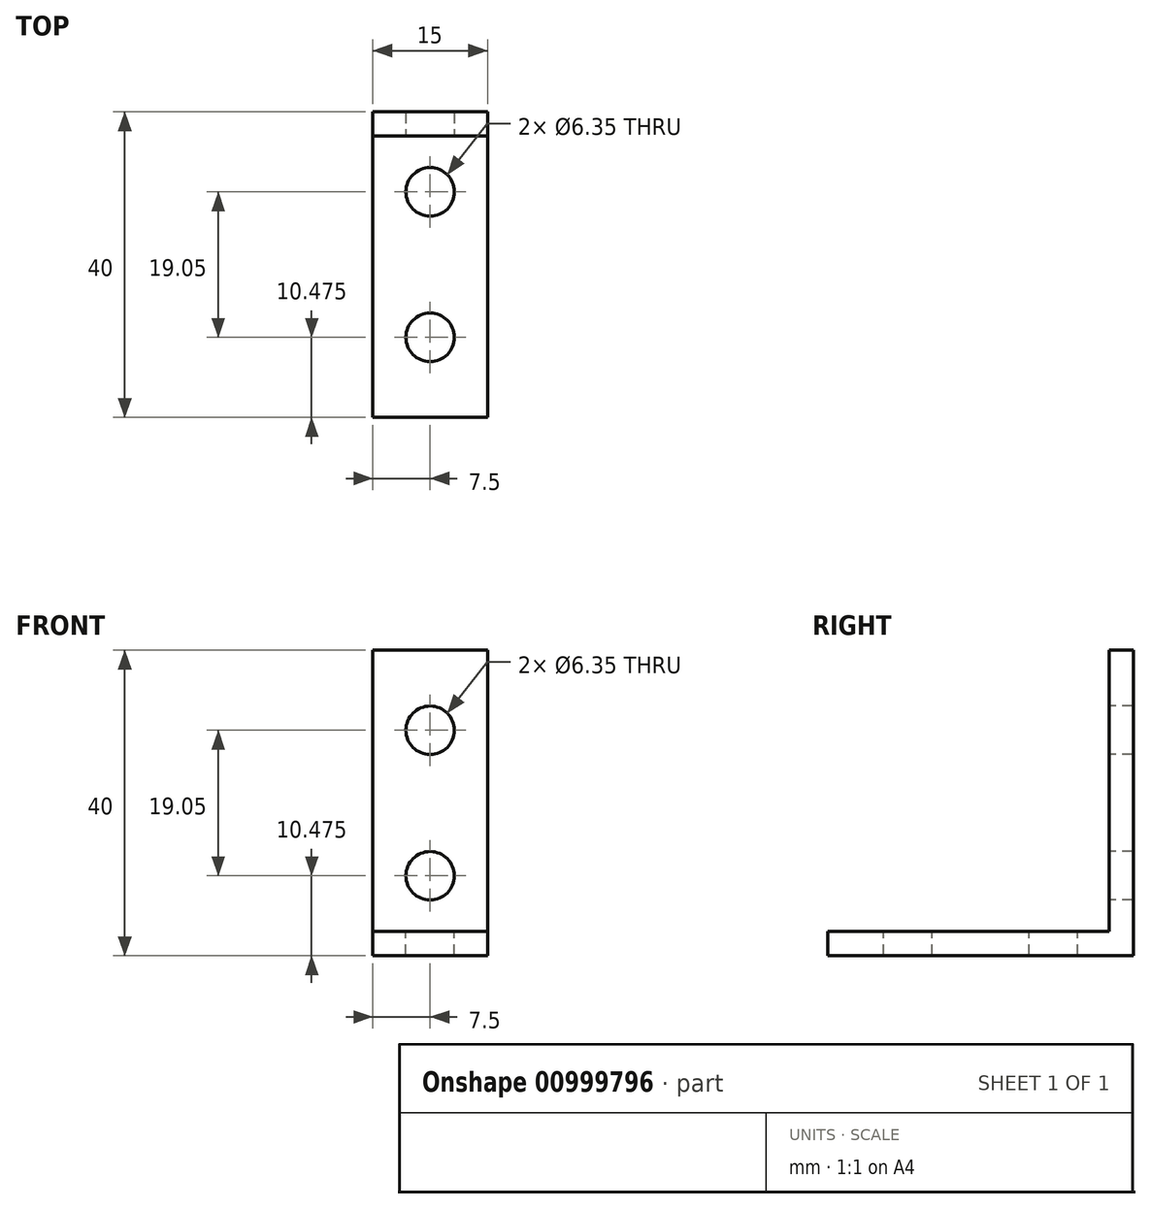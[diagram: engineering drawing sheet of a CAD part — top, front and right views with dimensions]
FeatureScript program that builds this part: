
annotation { "Feature Type Name" : "Feature", "Feature Type Description" : "" }
export const myFeature = defineFeature(function(context is Context, id is Id, definition is map)
    precondition{}
    {
        {
            var Q0;
            Q0=qCreatedBy(makeId("Right.planeOp"),FACE);
            var sketch = newSketch(context, id + "F0", { "sketchPlane" : qUnion([Q0])});
            skLineSegment(sketch, "E0.bottom", {"start": v(20, -20) * mm, "end": v(-20, -20) * mm});
            skLineSegment(sketch, "E0.top", {"start": v(20, 20) * mm, "end": v(16.82, 20) * mm});
            skLineSegment(sketch, "E0.left", {"start": v(20, -20) * mm, "end": v(20, 20) * mm});
            skLineSegment(sketch, "E0.right", {"start": v(-20, -20) * mm, "end": v(-20, -16.83) * mm});
            skPoint(sketch, "E0.middle", {"position": v(0, 0) * mm});
            skLineSegment(sketch, "E1.bottom", {"start": v(16.82, -16.82) * mm, "end": v(-16.83, -16.83) * mm});
            skLineSegment(sketch, "E1.left", {"start": v(16.82, -16.83) * mm, "end": v(16.82, 16.82) * mm});
            skLineSegment(sketch, "E2", {"start": v(-16.83, -16.83) * mm, "end": v(-20, -16.83) * mm});
            skLineSegment(sketch, "E3", {"start": v(16.82, 16.82) * mm, "end": v(16.82, 20) * mm});
            skPoint(sketch, "E1.right.end.orphan", {"position": v(-16.82, 16.82) * mm});
            skPoint(sketch, "E4.orphan", {"position": v(-20, 20) * mm});
            skSolve(sketch);
        }
        {
            var Q0;
            Q0=makeQuery(id+"F0.imprint","IMPRINT",FACE,{"disambiguationData":[TD([[makeQuery(id+"F0.imprint","IMPRINT",EDGE,{"derivedFrom":sQuery(id+"F0.wireOp",EDGE,"E0.bottom")}),-1.0]])]});
            extrude(context, id + "F1", {"entities" : qUnion([Q0]), "depth" : 15 * mm, "offsetDistance" : 25.4 * mm, "symmetric" : true});
        }
        {
            var Q0;
            Q0=makeQuery(id+"F1.opExtrude","SWEPT_FACE",FACE,{"disambiguationData":[OSD([sQuery(id+"F0.wireOp",EDGE,"E1.bottom"),sQuery(id+"F0.wireOp",EDGE,"E2")])]});
            var sketch = newSketch(context, id + "F2", { "sketchPlane" : qUnion([Q0])});
            skPoint(sketch, "E5.middle", {"position": v(0, 0) * mm});
            skCircle(sketch, "E6", {"center": v(0, 9.53) * mm, "radius": 3.18 * mm});
            skCircle(sketch, "E7", {"center": v(0, -9.53) * mm, "radius": 3.18 * mm});
            skSolve(sketch);
        }
        {
            var Q0;
            Q0=makeQuery(id+"F2.imprint","IMPRINT",FACE,{"disambiguationData":[TD([[makeQuery(id+"F2.imprint","IMPRINT",EDGE,{"derivedFrom":sQuery(id+"F2.wireOp",EDGE,"E6")}),1.0]])]});
            var Q1;
            Q1=makeQuery(id+"F2.imprint","IMPRINT",FACE,{"disambiguationData":[TD([[makeQuery(id+"F2.imprint","IMPRINT",EDGE,{"derivedFrom":sQuery(id+"F2.wireOp",EDGE,"E7")}),1.0]])]});
            extrude(context, id + "F3", {"entities" : qUnion([Q0, Q1]), "operationType" : NewBodyOperationType.REMOVE, "oppositeDirection" : true, "depth" : 10 * mm, "offsetDistance" : 25.4 * mm});
        }
        {
            var Q0;
            Q0=makeQuery(id+"F1.opExtrude","SWEPT_FACE",FACE,{"disambiguationData":[OSD([sQuery(id+"F0.wireOp",EDGE,"E1.left"),sQuery(id+"F0.wireOp",EDGE,"E3")])]});
            var sketch = newSketch(context, id + "F4", { "sketchPlane" : qUnion([Q0])});
            skPoint(sketch, "E8.middle", {"position": v(0, 0) * mm});
            skCircle(sketch, "E9", {"center": v(0, -9.53) * mm, "radius": 3.17 * mm});
            skCircle(sketch, "E10", {"center": v(0, 9.53) * mm, "radius": 3.17 * mm});
            skSolve(sketch);
        }
        {
            var Q0;
            Q0=makeQuery(id+"F4.imprint","IMPRINT",FACE,{"disambiguationData":[TD([[makeQuery(id+"F4.imprint","IMPRINT",EDGE,{"derivedFrom":sQuery(id+"F4.wireOp",EDGE,"E9")}),1.0]])]});
            var Q1;
            Q1=makeQuery(id+"F4.imprint","IMPRINT",FACE,{"disambiguationData":[TD([[makeQuery(id+"F4.imprint","IMPRINT",EDGE,{"derivedFrom":sQuery(id+"F4.wireOp",EDGE,"E10")}),1.0]])]});
            extrude(context, id + "F5", {"entities" : qUnion([Q0, Q1]), "operationType" : NewBodyOperationType.REMOVE, "oppositeDirection" : true, "depth" : 6.35 * mm, "offsetDistance" : 25.4 * mm});
        }
    });
